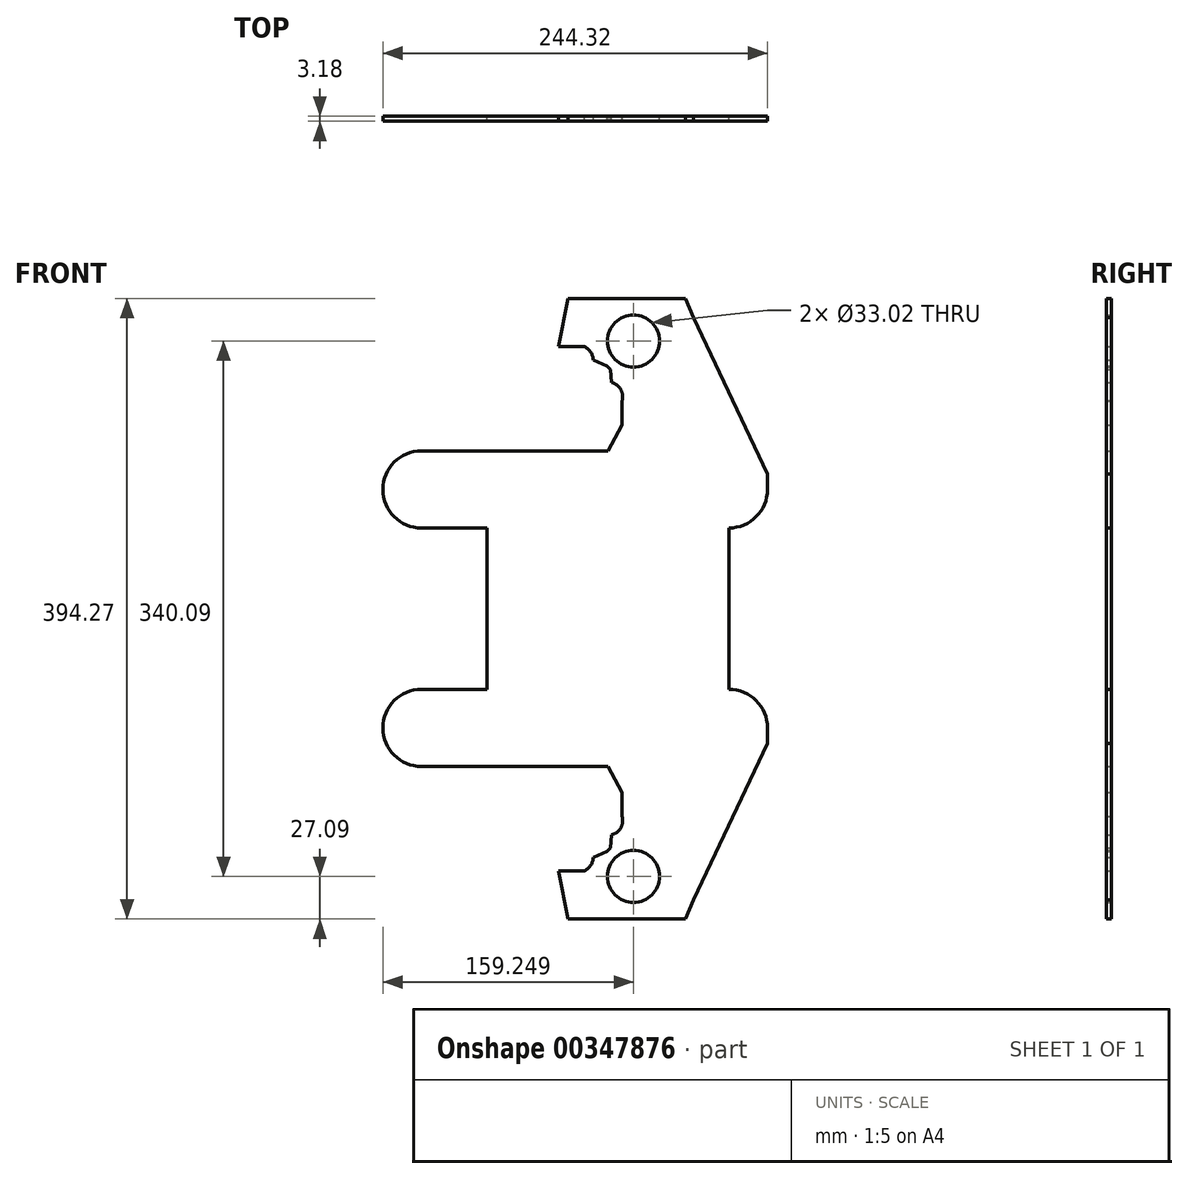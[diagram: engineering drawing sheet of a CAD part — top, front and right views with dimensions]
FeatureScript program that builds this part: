
annotation { "Feature Type Name" : "Feature", "Feature Type Description" : "" }
export const myFeature = defineFeature(function(context is Context, id is Id, definition is map)
    precondition{}
    {
        {
            var Q0;
            Q0=qCreatedBy(makeId("Front.planeOp"),FACE);
            var sketch = newSketch(context, id + "F0", { "sketchPlane" : qUnion([Q0])});
            skLineSegment(sketch, "E0", {"start": v(-81.45, -76.84) * mm, "end": v(72.17, -76.84) * mm, "construction": true});
            skLineSegment(sketch, "E1", {"start": v(72.17, -76.84) * mm, "end": v(72.17, -154.63) * mm});
            skLineSegment(sketch, "E2", {"start": v(72.17, -154.63) * mm, "end": v(-81.45, -154.63) * mm, "construction": true});
            skLineSegment(sketch, "E3", {"start": v(-81.45, -154.63) * mm, "end": v(-81.45, -76.84) * mm});
            skLineSegment(sketch, "E4", {"start": v(-81.45, -115.73) * mm, "end": v(72.17, -115.73) * mm, "construction": true});
            skLineSegment(sketch, "E5.MirrorCS", {"start": v(-4.64, -212.19) * mm, "end": v(-4.64, -205.84) * mm});
            skLineSegment(sketch, "E6.MirrorCS", {"start": v(-4.64, -177.14) * mm, "end": v(-4.64, -170.79) * mm});
            skLineSegment(sketch, "E7.MirrorCS", {"start": v(-7.82, -209.01) * mm, "end": v(-1.47, -209.01) * mm});
            skLineSegment(sketch, "E8.MirrorCS", {"start": v(-7.82, -173.96) * mm, "end": v(-1.47, -173.96) * mm});
            skLineSegment(sketch, "E9.MirrorCS", {"start": v(11.54, -256.65) * mm, "end": v(11.54, -250.3) * mm});
            skLineSegment(sketch, "E10.MirrorCS", {"start": v(36.3, -288.14) * mm, "end": v(36.3, -281.8) * mm});
            skLineSegment(sketch, "E11.MirrorCS", {"start": v(-4.64, -212.19) * mm, "end": v(-4.64, -215.94) * mm, "construction": true});
            skLineSegment(sketch, "E12.MirrorCS", {"start": v(-4.64, -173.96) * mm, "end": v(-4.64, -166.98) * mm, "construction": true});
            skLineSegment(sketch, "E13.MirrorCS", {"start": v(89.7, -194.66) * mm, "end": v(89.7, -188.31) * mm});
            skLineSegment(sketch, "E14.MirrorCS", {"start": v(86.52, -191.49) * mm, "end": v(92.87, -191.49) * mm});
            skLineSegment(sketch, "E15.MirrorCS", {"start": v(-16.5, -285) * mm, "end": v(-10.14, -285) * mm});
            skLineSegment(sketch, "E16.MirrorCS", {"start": v(-13.82, -276.18) * mm, "end": v(-7.47, -276.18) * mm});
            skLineSegment(sketch, "E17.MirrorCS", {"start": v(4.29, -247.72) * mm, "end": v(4.37, -247.82) * mm});
            skLineSegment(sketch, "E18.MirrorCS", {"start": v(-10.65, -279.36) * mm, "end": v(-10.65, -273) * mm});
            skArc(sketch, "E19.MirrorCS", {"start": v(-13.97, -273.64) * mm, "mid": v(-15.58, -278.63) * mm, "end": v(-19.49, -282.14) * mm});
            skLineSegment(sketch, "E20.MirrorCS", {"start": v(30.57, -293.7) * mm, "end": v(36.92, -293.7) * mm});
            skLineSegment(sketch, "E21.MirrorCS", {"start": v(82.71, -191.49) * mm, "end": v(96.68, -191.49) * mm, "construction": true});
            skArc(sketch, "E22.MirrorCS", {"start": v(-2.36, -259.37) * mm, "mid": v(3.44, -255.01) * mm, "end": v(4.37, -247.82) * mm});
            skLineSegment(sketch, "E23.MirrorCS", {"start": v(33.75, -296.87) * mm, "end": v(33.75, -290.52) * mm});
            skLineSegment(sketch, "E24.MirrorCS", {"start": v(5.8, -260.85) * mm, "end": v(5.8, -254.5) * mm});
            skLineSegment(sketch, "E25.MirrorCS", {"start": v(-13.32, -288.18) * mm, "end": v(-13.32, -281.83) * mm});
            skLineSegment(sketch, "E26.MirrorCS", {"start": v(33.12, -284.97) * mm, "end": v(39.47, -284.97) * mm});
            skLineSegment(sketch, "E27.MirrorCS", {"start": v(-5.4, -269.82) * mm, "end": v(-13.97, -273.64) * mm});
            skLineSegment(sketch, "E28.MirrorCS", {"start": v(8.37, -253.47) * mm, "end": v(14.72, -253.47) * mm});
            skLineSegment(sketch, "E29.MirrorCS", {"start": v(28.4, -256.7) * mm, "end": v(34.76, -256.7) * mm});
            skLineSegment(sketch, "E30.MirrorCS", {"start": v(-8.42, -303.17) * mm, "end": v(-2.07, -303.17) * mm});
            skLineSegment(sketch, "E31.MirrorCS", {"start": v(-2.36, -259.37) * mm, "end": v(-2.9, -267.57) * mm});
            skLineSegment(sketch, "E32.MirrorCS", {"start": v(-5.25, -306.34) * mm, "end": v(-5.25, -300) * mm});
            skLineSegment(sketch, "E33.MirrorCS", {"start": v(31.58, -259.87) * mm, "end": v(31.58, -253.52) * mm});
            skLineSegment(sketch, "E34.MirrorCS", {"start": v(24.91, -306.48) * mm, "end": v(31.26, -306.48) * mm});
            skLineSegment(sketch, "E35.MirrorCS", {"start": v(-2.04, -306.64) * mm, "end": v(4.31, -306.64) * mm});
            skLineSegment(sketch, "E36.MirrorCS", {"start": v(28.09, -309.66) * mm, "end": v(28.09, -303.3) * mm});
            skLineSegment(sketch, "E37.MirrorCS", {"start": v(-2.9, -267.57) * mm, "end": v(-5.4, -269.82) * mm});
            skPoint(sketch, "E38.MirrorP", {"position": v(-4.64, -173.96) * mm});
            skLineSegment(sketch, "E39.MirrorCS", {"start": v(96.68, -191.49) * mm, "end": v(96.68, -201.41) * mm});
            skLineSegment(sketch, "E40.MirrorCS", {"start": v(-19.49, -282.14) * mm, "end": v(-36, -282.15) * mm});
            skLineSegment(sketch, "E41.MirrorCS", {"start": v(4.29, -232.48) * mm, "end": v(-4.64, -215.94) * mm});
            skLineSegment(sketch, "E42.MirrorCS", {"start": v(44.47, -312.87) * mm, "end": v(49.8, -300.57) * mm});
            skLineSegment(sketch, "E43.MirrorCS", {"start": v(4.29, -247.72) * mm, "end": v(4.29, -232.48) * mm});
            skPoint(sketch, "E44.MirrorP", {"position": v(-5.25, -303.17) * mm});
            skPoint(sketch, "E45.MirrorP", {"position": v(-10.65, -276.18) * mm});
            skLineSegment(sketch, "E46.MirrorCS", {"start": v(-4.64, -170.79) * mm, "end": v(-4.64, -212.19) * mm, "construction": true});
            skPoint(sketch, "E47.MirrorP", {"position": v(-4.64, -209.01) * mm});
            skPoint(sketch, "E48.MirrorP", {"position": v(1.14, -306.64) * mm});
            skPoint(sketch, "E49.MirrorP", {"position": v(11.54, -253.47) * mm});
            skPoint(sketch, "E50.MirrorP", {"position": v(33.75, -293.7) * mm});
            skPoint(sketch, "E51.MirrorP", {"position": v(31.58, -256.7) * mm});
            skPoint(sketch, "E52.MirrorP", {"position": v(28.09, -306.48) * mm});
            skPoint(sketch, "E53.MirrorP", {"position": v(-13.32, -285) * mm});
            skPoint(sketch, "E54.MirrorP", {"position": v(36.3, -284.97) * mm});
            skPoint(sketch, "E55.MirrorP", {"position": v(89.7, -191.49) * mm});
            skPoint(sketch, "E56.MirrorP", {"position": v(86.8, -191.49) * mm});
            skArc(sketch, "E57.MirrorCS", {"start": v(72.17, -166.98) * mm, "mid": v(89.5, -174.15) * mm, "end": v(96.68, -191.49) * mm});
            skLineSegment(sketch, "E58.MirrorCS", {"start": v(-4.64, -166.98) * mm, "end": v(72.17, -166.98) * mm, "construction": true});
            skLineSegment(sketch, "E59.MirrorCS", {"start": v(-29.95, -312.87) * mm, "end": v(-36, -282.15) * mm});
            skPoint(sketch, "E60.MirrorP", {"position": v(-10.8, -260.27) * mm});
            skLineSegment(sketch, "E61.MirrorCS", {"start": v(49.8, -300.57) * mm, "end": v(96.68, -201.41) * mm});
            skCircle(sketch, "E62.MirrorC", {"center": v(11.6, -285.78) * mm, "radius": 16.51 * mm});
            skLineSegment(sketch, "E63.MirrorCS", {"start": v(-29.95, -312.87) * mm, "end": v(44.47, -312.87) * mm});
            skLineSegment(sketch, "E64", {"start": v(72.17, -166.98) * mm, "end": v(72.17, -154.63) * mm});
            skLineSegment(sketch, "E65", {"start": v(1.14, -309.81) * mm, "end": v(1.14, -303.46) * mm});
            skLineSegment(sketch, "E66.MirrorCS", {"start": v(2.62, -257.68) * mm, "end": v(8.97, -257.68) * mm});
            skPoint(sketch, "E67", {"position": v(5.8, -257.68) * mm});
            skPoint(sketch, "E68", {"position": v(-105.63, -191.46) * mm});
            skLineSegment(sketch, "E69", {"start": v(-105.63, -191.46) * mm, "end": v(-123.15, -191.46) * mm, "construction": true});
            skLineSegment(sketch, "E70", {"start": v(-123.15, -215.94) * mm, "end": v(-123.15, -166.98) * mm, "construction": true});
            skLineSegment(sketch, "E71", {"start": v(-123.15, -166.98) * mm, "end": v(-4.64, -166.98) * mm, "construction": true});
            skArc(sketch, "E72", {"start": v(-123.15, -215.94) * mm, "mid": v(-147.64, -191.46) * mm, "end": v(-123.15, -166.98) * mm});
            skLineSegment(sketch, "E73", {"start": v(-123.15, -215.94) * mm, "end": v(-4.64, -215.94) * mm});
            skLineSegment(sketch, "E74", {"start": v(-81.45, -154.63) * mm, "end": v(-81.45, -166.98) * mm});
            skLineSegment(sketch, "E75", {"start": v(-81.45, -166.98) * mm, "end": v(-123.15, -166.98) * mm});
            skLineSegment(sketch, "E76.MirrorCS", {"start": v(-126.33, -191.46) * mm, "end": v(-119.98, -191.46) * mm});
            skLineSegment(sketch, "E77.MirrorCS", {"start": v(-123.15, -194.63) * mm, "end": v(-123.15, -188.28) * mm});
            skLineSegment(sketch, "E78.MirrorCS", {"start": v(-123.15, -36.84) * mm, "end": v(-123.15, -43.19) * mm});
            skLineSegment(sketch, "E79.MirrorCS", {"start": v(-126.33, -40.01) * mm, "end": v(-119.98, -40.01) * mm});
            skLineSegment(sketch, "E80.MirrorCS", {"start": v(1.14, 78.35) * mm, "end": v(1.14, 72) * mm});
            skLineSegment(sketch, "E81.MirrorCS", {"start": v(-2.04, 75.17) * mm, "end": v(4.31, 75.17) * mm});
            skLineSegment(sketch, "E82.MirrorCS", {"start": v(-4.64, -19.28) * mm, "end": v(-4.64, -25.63) * mm});
            skLineSegment(sketch, "E83.MirrorCS", {"start": v(-4.64, -54.33) * mm, "end": v(-4.64, -60.68) * mm});
            skLineSegment(sketch, "E84.MirrorCS", {"start": v(-7.82, -22.46) * mm, "end": v(-1.47, -22.46) * mm});
            skLineSegment(sketch, "E85.MirrorCS", {"start": v(-7.82, -57.5) * mm, "end": v(-1.47, -57.5) * mm});
            skLineSegment(sketch, "E86.MirrorCS", {"start": v(-4.64, -57.5) * mm, "end": v(-4.64, -64.5) * mm, "construction": true});
            skLineSegment(sketch, "E87.MirrorCS", {"start": v(-4.64, -19.28) * mm, "end": v(-4.64, -15.53) * mm, "construction": true});
            skLineSegment(sketch, "E88.MirrorCS", {"start": v(-5.25, 74.88) * mm, "end": v(-5.25, 68.53) * mm});
            skLineSegment(sketch, "E89.MirrorCS", {"start": v(-8.42, 71.7) * mm, "end": v(-2.07, 71.7) * mm});
            skLineSegment(sketch, "E90.MirrorCS", {"start": v(4.29, 16.25) * mm, "end": v(4.37, 16.35) * mm});
            skLineSegment(sketch, "E91.MirrorCS", {"start": v(89.7, -36.8) * mm, "end": v(89.7, -43.16) * mm});
            skLineSegment(sketch, "E92.MirrorCS", {"start": v(86.52, -39.98) * mm, "end": v(92.87, -39.98) * mm});
            skLineSegment(sketch, "E93.MirrorCS", {"start": v(-16.5, 53.53) * mm, "end": v(-10.14, 53.53) * mm});
            skLineSegment(sketch, "E94.MirrorCS", {"start": v(11.54, 25.18) * mm, "end": v(11.54, 18.83) * mm});
            skLineSegment(sketch, "E95.MirrorCS", {"start": v(36.3, 56.67) * mm, "end": v(36.3, 50.32) * mm});
            skLineSegment(sketch, "E96.MirrorCS", {"start": v(2.62, 26.2) * mm, "end": v(8.97, 26.2) * mm});
            skLineSegment(sketch, "E97.MirrorCS", {"start": v(-13.82, 44.71) * mm, "end": v(-7.47, 44.71) * mm});
            skLineSegment(sketch, "E98.MirrorCS", {"start": v(8.37, 22) * mm, "end": v(14.72, 22) * mm});
            skLineSegment(sketch, "E99.MirrorCS", {"start": v(5.8, 29.38) * mm, "end": v(5.8, 23.03) * mm});
            skLineSegment(sketch, "E100.MirrorCS", {"start": v(33.12, 53.5) * mm, "end": v(39.47, 53.5) * mm});
            skLineSegment(sketch, "E101.MirrorCS", {"start": v(-13.32, 56.7) * mm, "end": v(-13.32, 50.36) * mm});
            skArc(sketch, "E102.MirrorCS", {"start": v(-2.36, 27.9) * mm, "mid": v(3.44, 23.54) * mm, "end": v(4.37, 16.35) * mm});
            skArc(sketch, "E103.MirrorCS", {"start": v(-13.97, 42.17) * mm, "mid": v(-15.58, 47.16) * mm, "end": v(-19.49, 50.67) * mm});
            skPoint(sketch, "E104.MirrorP", {"position": v(1.14, 75.17) * mm});
            skLineSegment(sketch, "E105.MirrorCS", {"start": v(-5.4, 38.35) * mm, "end": v(-13.97, 42.17) * mm});
            skLineSegment(sketch, "E106.MirrorCS", {"start": v(33.75, 65.4) * mm, "end": v(33.75, 59.05) * mm});
            skLineSegment(sketch, "E107.MirrorCS", {"start": v(30.57, 62.23) * mm, "end": v(36.92, 62.23) * mm});
            skLineSegment(sketch, "E108.MirrorCS", {"start": v(28.4, 25.22) * mm, "end": v(34.76, 25.22) * mm});
            skPoint(sketch, "E109.MirrorP", {"position": v(-123.15, -40.01) * mm});
            skLineSegment(sketch, "E110.MirrorCS", {"start": v(-10.65, 47.89) * mm, "end": v(-10.65, 41.54) * mm});
            skLineSegment(sketch, "E111.MirrorCS", {"start": v(82.71, -39.98) * mm, "end": v(96.68, -39.98) * mm, "construction": true});
            skLineSegment(sketch, "E112.MirrorCS", {"start": v(-2.9, 36.1) * mm, "end": v(-5.4, 38.35) * mm});
            skLineSegment(sketch, "E113.MirrorCS", {"start": v(31.58, 28.4) * mm, "end": v(31.58, 22.05) * mm});
            skLineSegment(sketch, "E114.MirrorCS", {"start": v(72.17, -64.5) * mm, "end": v(72.17, -76.84) * mm});
            skLineSegment(sketch, "E115.MirrorCS", {"start": v(28.09, 78.19) * mm, "end": v(28.09, 71.84) * mm});
            skLineSegment(sketch, "E116.MirrorCS", {"start": v(-81.45, -76.84) * mm, "end": v(-81.45, -64.5) * mm});
            skLineSegment(sketch, "E117.MirrorCS", {"start": v(4.29, 16.25) * mm, "end": v(4.29, 1.01) * mm});
            skLineSegment(sketch, "E118.MirrorCS", {"start": v(-105.63, -40.01) * mm, "end": v(-123.15, -40.01) * mm, "construction": true});
            skPoint(sketch, "E119.MirrorP", {"position": v(-4.64, -57.5) * mm});
            skLineSegment(sketch, "E120.MirrorCS", {"start": v(44.47, 81.4) * mm, "end": v(49.8, 69.1) * mm});
            skLineSegment(sketch, "E121.MirrorCS", {"start": v(96.68, -39.98) * mm, "end": v(96.68, -30.06) * mm});
            skLineSegment(sketch, "E122.MirrorCS", {"start": v(-2.36, 27.9) * mm, "end": v(-2.9, 36.1) * mm});
            skLineSegment(sketch, "E123.MirrorCS", {"start": v(24.91, 75.01) * mm, "end": v(31.26, 75.01) * mm});
            skPoint(sketch, "E124.MirrorP", {"position": v(-4.64, -22.46) * mm});
            skPoint(sketch, "E125.MirrorP", {"position": v(31.58, 25.22) * mm});
            skPoint(sketch, "E126.MirrorP", {"position": v(-5.25, 71.7) * mm});
            skPoint(sketch, "E127.MirrorP", {"position": v(5.8, 26.2) * mm});
            skPoint(sketch, "E128.MirrorP", {"position": v(11.54, 22) * mm});
            skPoint(sketch, "E129.MirrorP", {"position": v(33.75, 62.23) * mm});
            skPoint(sketch, "E130.MirrorP", {"position": v(36.3, 53.5) * mm});
            skLineSegment(sketch, "E131.MirrorCS", {"start": v(-81.45, -64.5) * mm, "end": v(-123.15, -64.5) * mm});
            skPoint(sketch, "E132.MirrorP", {"position": v(89.7, -39.98) * mm});
            skPoint(sketch, "E133.MirrorP", {"position": v(-10.8, 28.8) * mm});
            skPoint(sketch, "E134.MirrorP", {"position": v(-10.65, 44.71) * mm});
            skPoint(sketch, "E135.MirrorP", {"position": v(-13.32, 53.53) * mm});
            skLineSegment(sketch, "E136.MirrorCS", {"start": v(-4.64, -60.68) * mm, "end": v(-4.64, -19.28) * mm, "construction": true});
            skLineSegment(sketch, "E137.MirrorCS", {"start": v(-123.15, -64.5) * mm, "end": v(-4.64, -64.5) * mm, "construction": true});
            skLineSegment(sketch, "E138.MirrorCS", {"start": v(-19.49, 50.67) * mm, "end": v(-36, 50.68) * mm});
            skLineSegment(sketch, "E139.MirrorCS", {"start": v(-123.15, -15.53) * mm, "end": v(-123.15, -64.5) * mm, "construction": true});
            skLineSegment(sketch, "E140.MirrorCS", {"start": v(-4.64, -64.5) * mm, "end": v(72.17, -64.5) * mm, "construction": true});
            skCircle(sketch, "E141.MirrorC", {"center": v(11.6, 54.31) * mm, "radius": 16.51 * mm});
            skPoint(sketch, "E142.MirrorP", {"position": v(28.09, 75.01) * mm});
            skPoint(sketch, "E143.MirrorP", {"position": v(-105.63, -40.01) * mm});
            skArc(sketch, "E144.MirrorCS", {"start": v(72.17, -64.5) * mm, "mid": v(89.5, -57.32) * mm, "end": v(96.68, -39.98) * mm});
            skArc(sketch, "E145.MirrorCS", {"start": v(-123.15, -15.53) * mm, "mid": v(-147.64, -40.01) * mm, "end": v(-123.15, -64.5) * mm});
            skLineSegment(sketch, "E146.MirrorCS", {"start": v(4.29, 1.01) * mm, "end": v(-4.64, -15.53) * mm});
            skLineSegment(sketch, "E147.MirrorCS", {"start": v(-29.95, 81.4) * mm, "end": v(-36, 50.68) * mm});
            skLineSegment(sketch, "E148.MirrorCS", {"start": v(-29.95, 81.4) * mm, "end": v(44.47, 81.4) * mm});
            skLineSegment(sketch, "E149.MirrorCS", {"start": v(-123.15, -15.53) * mm, "end": v(-4.64, -15.53) * mm});
            skLineSegment(sketch, "E150.MirrorCS", {"start": v(49.8, 69.1) * mm, "end": v(96.68, -30.06) * mm});
            skPoint(sketch, "E151.MirrorP", {"position": v(86.8, -39.98) * mm});
            skSolve(sketch);
        }
        {
            var Q0;
            Q0=makeQuery(id+"F0.imprint","IMPRINT",FACE,{"disambiguationData":[TD([[makeQuery(id+"F0.imprint","IMPRINT",EDGE,{"derivedFrom":sQuery(id+"F0.wireOp",EDGE,"hgDJoyhs-avOh-k2XS-gEzC-Oh4LszvJW2BN")}),-1.0]])]});
            var Q1;
            Q1=qSketchRegion(id+"F0",true);
            extrude(context, id + "F1", {"entities" : qUnion([Q0, Q1]), "depth" : 3.17 * mm});
        }
    });
